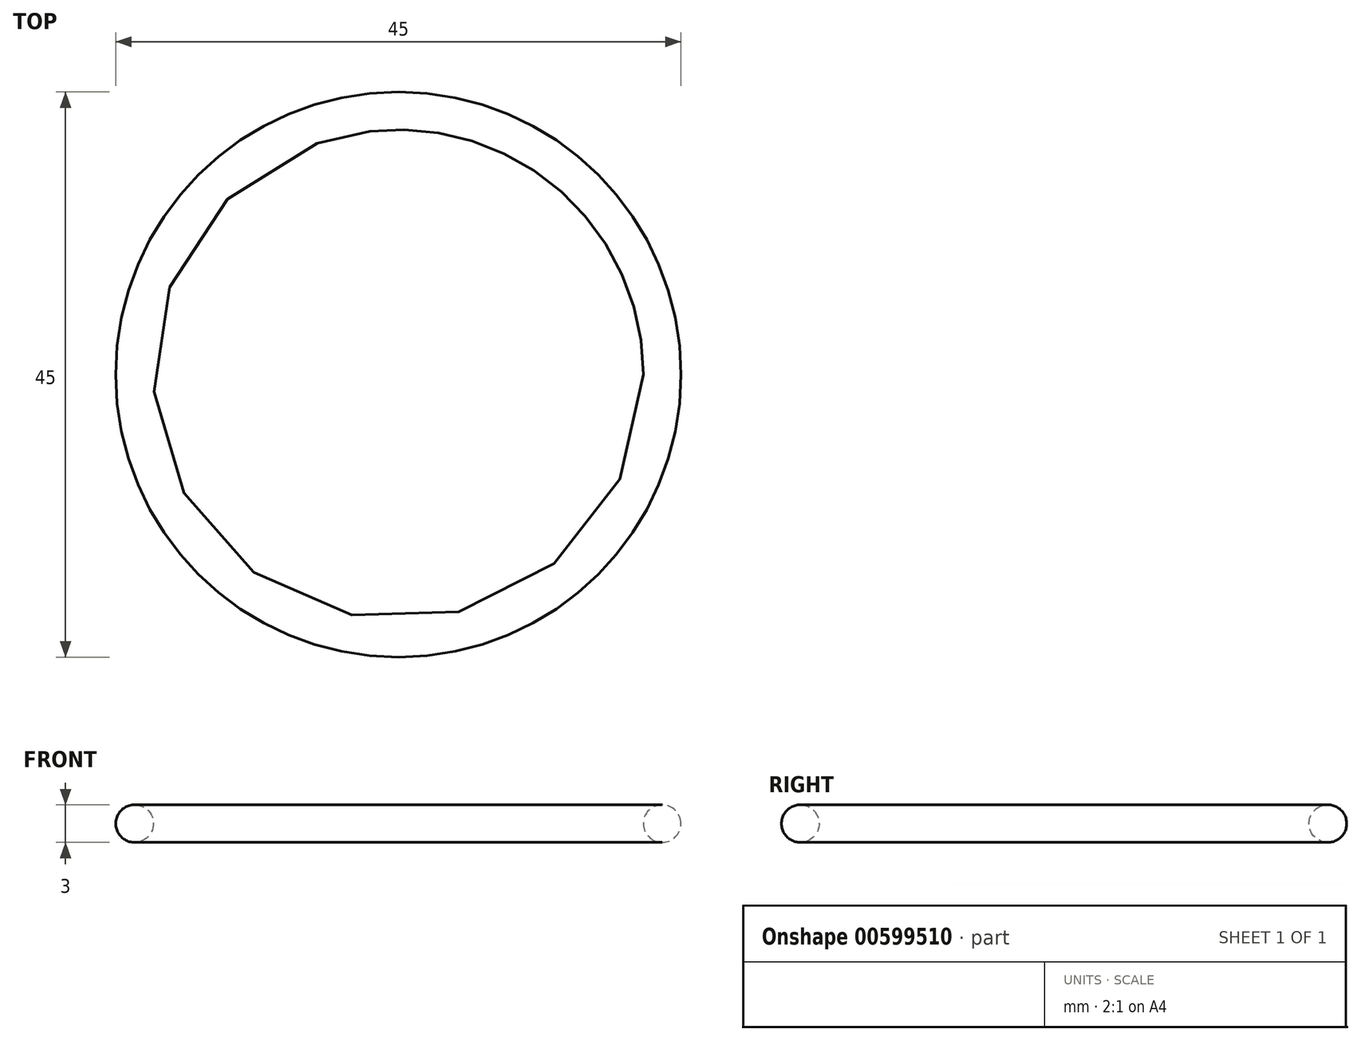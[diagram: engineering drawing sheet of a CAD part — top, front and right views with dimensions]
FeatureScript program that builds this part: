
annotation { "Feature Type Name" : "Feature", "Feature Type Description" : "" }
export const myFeature = defineFeature(function(context is Context, id is Id, definition is map)
    precondition{}
    {
        {
            var Q0;
            Q0=qCreatedBy(makeId("Front.planeOp"),FACE);
            var sketch = newSketch(context, id + "F0", { "sketchPlane" : qUnion([Q0])});
            skLineSegment(sketch, "E0", {"start": v(0, 5.91) * mm, "end": v(0, 0) * mm, "construction": true});
            skLineSegment(sketch, "E1", {"start": v(0, 0) * mm, "end": v(-21, 0) * mm, "construction": true});
            skCircle(sketch, "E2", {"center": v(-21, 0) * mm, "radius": 1.5 * mm});
            skSolve(sketch);
        }
        {
            var Q0;
            Q0 = qSketchRegion(id + "F0", true);
            var Q1;
            Q1=sQuery(id+"F0.wireOp",EDGE,"E0");
            revolve(context, id + "F1", {"entities" : qUnion([Q0]), "axis" : qUnion([Q1]), "revolveType" : RevolveType.FULL});
        }
    });
